# Revit family: Landscaping_Other_Axelent_Bull-Hanger
name_source: partatom
category: Furniture
revit_build: Autodesk Revit 2018 (Build: 20170223_1515(x64)
units: mm (PartAtom-declared; Revit-internal decimal feet)

## family parameters
Always vertical = Yes
Cut with Voids When Loaded = No
OmniClass Number = 23.40.10.14
OmniClass Title = Exterior Specialties
Room Calculation Point = No
Shared = No
Work Plane-Based = No

## types (4) — shared parameters
AssetType = Fixed
BIMObjectName = Landscaping_Other_Axelent_Bull-Hanger
Brand = Axelent
Category = Cycle lockers
Color = Galvanized
CycleBollardMainMaterial = Steel, Galvanized
Description = Bull Hanger is a single bike rack placed on the wall, where you can hang the bike on two hooks.The two hooks can be pulled to suitable width depending on size and model of the bike.
IfcExportAs = IfcFurnishingElementType
IfcExportType = BOLLARD
MainColor = Galvanized
Manufacturer = Axelent
ManufacturerName = Axelent
ManufacturerURL = https://www.axelent.com
Material = Steel
ModelNumber = 102030
NBSDescription = Aluminium cycle lockers
NBSReference = 45-35-86/311
Name = Bull-Hanger
NominalHeight = 280 mm  [stored 0.918635 ft]
ProductDatasheet = https://www.axelent.com
ProductInformation = Bull Hanger is a single bike rack placed on the wall, where you can hang the bike on two hooks.The two hooks can be pulled to suitable width depending on size and model of the bike.
Shape = Sculptured
URL = https://www.axelent.com
Uniclass2 = Pr_40_30_20
Uniclass2015Description = Cycle stands and lockers
Uniclass2015Reference = Pr_40_30_21
Version = 1
VersionDate = 28/03/2022
WarrantyDurationUnit = Years
zero-valued in all types: Cost

## per-type parameters (varying)
| type | DurationUnit | ExpectedLife | NominalDepth | NominalLength | Size | bull type |
| Bull Narrow |  | Years | 400 mm | 320 mm | 320x400x280 mm | bull small |
| Bull Medium | Yeras |  | 390 mm | 420 mm | 420x390x280 mm | bull mediuml |
| Bull Wide | Yeras |  | 350 mm | 520 mm | 520x350x280 mm | bull large |
| Bull Extra Wide | Yeras |  | 100 mm  [stored 0.328084 ft] | 900 mm | 900x100x280 mm | bull extra large |

note: column(s) folded — value = type name in every type: Model

note: [stored X ft] marks values corroborated as IEEE doubles in the binary element streams (Revit-internal decimal feet)

## geometry (parser evidence)
native form markers: Sweep x10
no freeform markers — native parametric forms only
